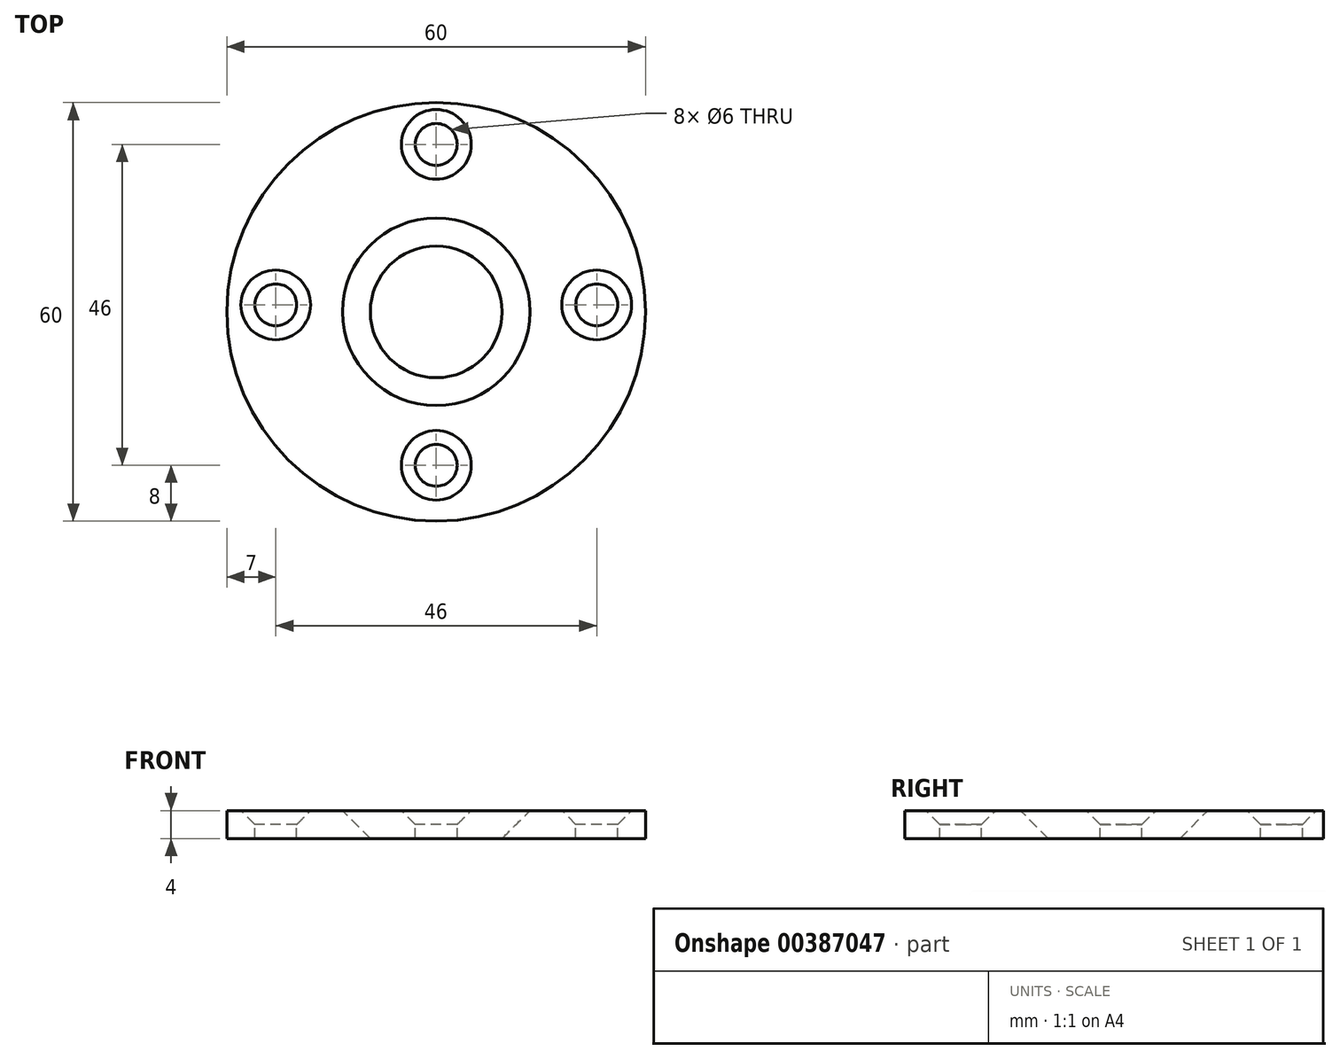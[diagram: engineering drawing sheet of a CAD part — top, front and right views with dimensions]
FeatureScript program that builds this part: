
annotation { "Feature Type Name" : "Feature", "Feature Type Description" : "" }
export const myFeature = defineFeature(function(context is Context, id is Id, definition is map)
    precondition{}
    {
        {
            var Q0;
            Q0=qCreatedBy(makeId("Top.planeOp"),FACE);
            var sketch = newSketch(context, id + "F0", { "sketchPlane" : qUnion([Q0])});
            skCircle(sketch, "E0", {"center": v(0, 0) * mm, "radius": 30 * mm});
            skLineSegment(sketch, "E1", {"start": v(0, 58.35) * mm, "end": v(0, -77.4) * mm, "construction": true});
            skLineSegment(sketch, "E2", {"start": v(-51.81, 0) * mm, "end": v(72.58, 0) * mm, "construction": true});
            skSolve(sketch);
        }
        {
            var Q0;
            Q0 = qSketchRegion(id + "F0", true);
            extrude(context, id + "F1", {"entities" : qUnion([Q0]), "oppositeDirection" : true, "depth" : 4 * mm});
        }
        {
            var Q0;
            Q0=makeQuery(id+"F1.opExtrude","CAP_FACE",FACE,{"disambiguationData":[OSD([sQuery(id+"F0.wireOp",EDGE,"E0")])],"isStart":true});
            var sketch = newSketch(context, id + "F2", { "sketchPlane" : qUnion([Q0])});
            skPoint(sketch, "E3", {"position": v(0, 0) * mm});
            skLineSegment(sketch, "E4.anchor1", {"start": v(0, 0) * mm, "end": v(0, 25) * mm, "construction": true});
            skLineSegment(sketch, "E4.anchor2", {"start": v(0, 0) * mm, "end": v(25, 0) * mm, "construction": true});
            skSolve(sketch);
        }
        {
            var Q0;
            Q0=sQuery(id+"F2.wireOp",VERTEX,"E3");
            var Q1;
            Q1=makeQuery(id+"F1.opExtrude","SWEPT_BODY",BODY,{"disambiguationData":[OSD([sQuery(id+"F0.wireOp",EDGE,"E0")])]});
            hole(context, id + "F3", {"style" : HoleStyle.C_SINK, "endStyle" : HoleEndStyle.BLIND, "standardTappedOrClearance" : lookupTablePath({ "standard" : "ISO", "fit" : "Normal", "size" : "M12", "type" : "Clearance" }), "standardBlindInLast" : lookupTablePath({ "fit" : "Standard", "standard" : "ISO", "size" : "M12", "type" : "Clearance" }), "holeDiameter" : 13.2 * mm, "cSinkDiameter" : 26.88 * mm, "cSinkAngle" : 90 * degree, "holeDepth" : 12 * mm, "isTappedThrough" : true, "tappedDepth" : 12 * mm, "tapClearance" : 3, "startFromSketch" : true, "locations" : qUnion([Q0]), "scope" : qUnion([Q1])});
        }
        {
            var Q0;
            Q0=makeQuery(id+"F1.opExtrude","CAP_FACE",FACE,{"disambiguationData":[OSD([sQuery(id+"F0.wireOp",EDGE,"E0")])],"isStart":true});
            var sketch = newSketch(context, id + "F4", { "sketchPlane" : qUnion([Q0])});
            skPoint(sketch, "E5", {"position": v(0, 24) * mm});
            skPoint(sketch, "E6.1.0", {"position": v(-23, 1) * mm});
            skPoint(sketch, "E6.2.0", {"position": v(0, -22) * mm});
            skPoint(sketch, "E6.3.0", {"position": v(23, 1) * mm});
            skPoint(sketch, "E6.center", {"position": v(0, 1) * mm});
            skSolve(sketch);
        }
        {
            var Q0;
            Q0=sQuery(id+"F4.wireOp",VERTEX,"E6.1.0");
            var Q1;
            Q1=sQuery(id+"F4.wireOp",VERTEX,"E5");
            var Q2;
            Q2=sQuery(id+"F4.wireOp",VERTEX,"E6.3.0");
            var Q3;
            Q3=sQuery(id+"F4.wireOp",VERTEX,"E6.2.0");
            var Q4;
            Q4=makeQuery(id+"F1.opExtrude","SWEPT_BODY",BODY,{"disambiguationData":[OSD([sQuery(id+"F0.wireOp",EDGE,"E0")])]});
            hole(context, id + "F5", {"style" : HoleStyle.C_SINK, "endStyle" : HoleEndStyle.BLIND, "holeDiameter" : 6 * mm, "cSinkDiameter" : 10 * mm, "cSinkAngle" : 90 * degree, "holeDepth" : 12 * mm, "isTappedThrough" : true, "tappedDepth" : 12 * mm, "tapClearance" : 3, "startFromSketch" : true, "locations" : qUnion([Q0, Q1, Q2, Q3]), "scope" : qUnion([Q4])});
        }
    });
